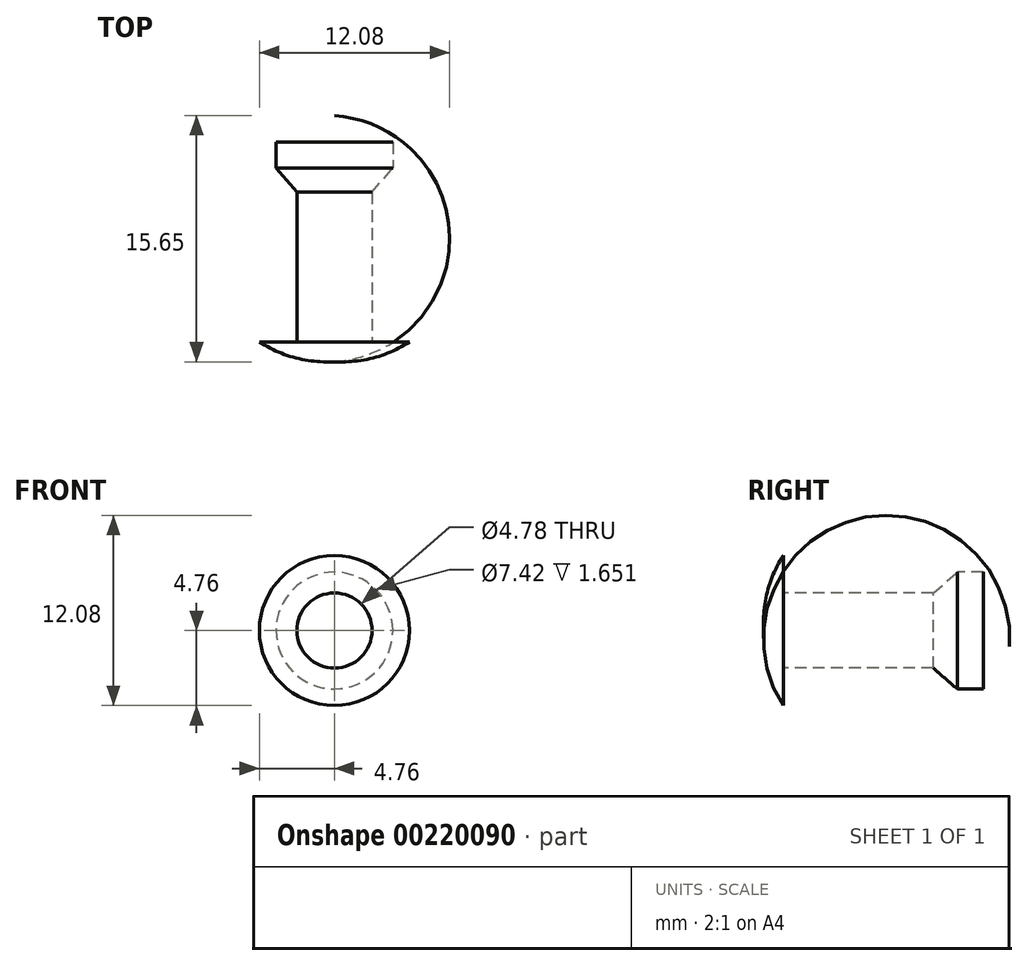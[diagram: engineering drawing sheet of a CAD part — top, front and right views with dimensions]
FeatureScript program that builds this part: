
annotation { "Feature Type Name" : "Feature", "Feature Type Description" : "" }
export const myFeature = defineFeature(function(context is Context, id is Id, definition is map)
    precondition{}
    {
        {
            var Q0;
            Q0=qCreatedBy(makeId("Right.planeOp"),FACE);
            var sketch = newSketch(context, id + "F0", { "sketchPlane" : qUnion([Q0])});
            skLineSegment(sketch, "E0", {"start": v(-1.52, 0) * mm, "end": v(12.7, 0) * mm});
            skLineSegment(sketch, "E1", {"start": v(-0.28, 2.39) * mm, "end": v(9.24, 2.39) * mm});
            skPoint(sketch, "E2", {"position": v(-1.52, 0) * mm});
            skLineSegment(sketch, "E3", {"start": v(-0.28, 2.39) * mm, "end": v(-0.28, 4.76) * mm});
            skArc(sketch, "E4", {"start": v(-0.28, 4.76) * mm, "mid": v(-1.29, 2.48) * mm, "end": v(-1.52, 0) * mm});
            skLineSegment(sketch, "E5", {"start": v(9.24, 2.39) * mm, "end": v(10.77, 3.7) * mm});
            skLineSegment(sketch, "E6", {"start": v(12.42, 3.7) * mm, "end": v(12.42, 0) * mm});
            skLineSegment(sketch, "E7", {"start": v(12.7, 0) * mm, "end": v(12.42, 0) * mm});
            skLineSegment(sketch, "E8", {"start": v(10.77, 3.7) * mm, "end": v(12.42, 3.7) * mm});
            skPoint(sketch, "E8.startSnap0", {"position": v(10.77, 3.7) * mm});
            skSolve(sketch);
        }
        {
            var Q0;
            Q0=qSketchRegion(id+"F0",true);
            var Q1;
            Q1=sQuery(id+"F0.wireOp",EDGE,"E0");
            revolve(context, id + "F1", {"entities" : qUnion([Q0]), "axis" : qUnion([Q1]), "revolveType" : RevolveType.FULL});
        }
    });
